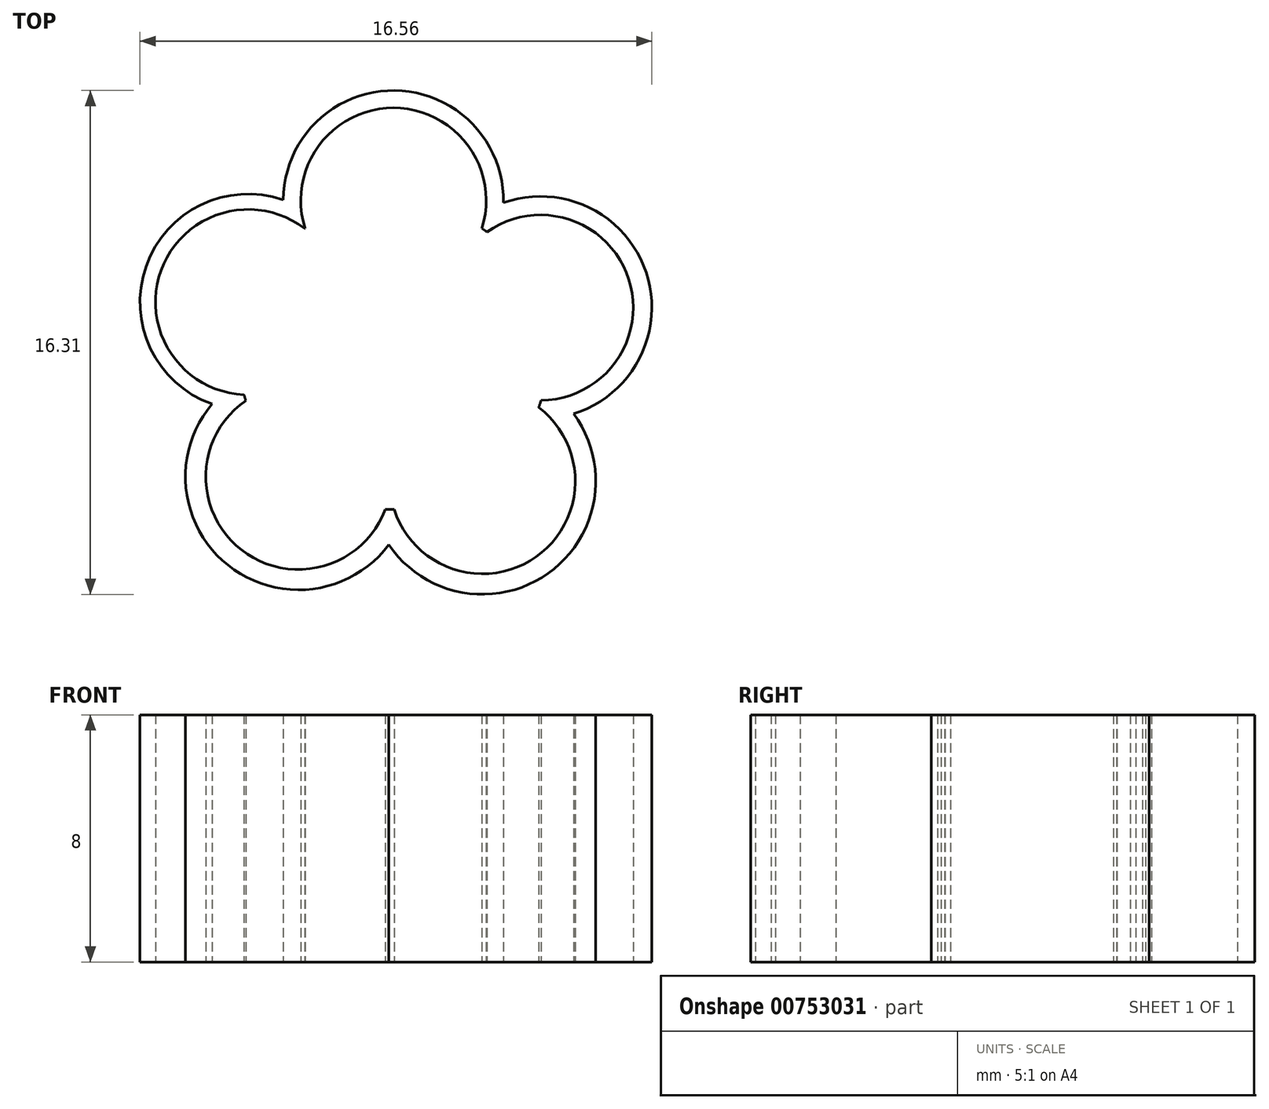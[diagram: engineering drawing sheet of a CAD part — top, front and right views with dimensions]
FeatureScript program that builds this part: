
annotation { "Feature Type Name" : "Feature", "Feature Type Description" : "" }
export const myFeature = defineFeature(function(context is Context, id is Id, definition is map)
    precondition{}
    {
        {
            var Q0;
            Q0=qCreatedBy(makeId("Top.planeOp"),FACE);
            var sketch = newSketch(context, id + "F0", { "sketchPlane" : qUnion([Q0])});
            skArc(sketch, "E0", {"start": v(-4.83, -1.29) * mm, "mid": v(-4.8, -1.38) * mm, "end": v(-4.78, -1.48) * mm});
            skArc(sketch, "E1", {"start": v(-2.85, 4.08) * mm, "mid": v(-7.51, 2.75) * mm, "end": v(-4.83, -1.29) * mm});
            skArc(sketch, "E2.trimOffspring", {"start": v(-2.86, 4.1) * mm, "mid": v(-2.87, 4.1) * mm, "end": v(-2.87, 4.1) * mm});
            skArc(sketch, "E3.trimOffspring", {"start": v(2.86, 4.1) * mm, "mid": v(-0.01, 8) * mm, "end": v(-2.85, 4.08) * mm});
            skArc(sketch, "E4.trimOffspring", {"start": v(4.78, -1.47) * mm, "mid": v(7.61, 2.45) * mm, "end": v(3.02, 3.98) * mm});
            skArc(sketch, "E5.trimOffspring", {"start": v(4.7, -1.7) * mm, "mid": v(4.74, -1.58) * mm, "end": v(4.78, -1.47) * mm});
            skArc(sketch, "E6.trimOffspring", {"start": v(3.02, 3.98) * mm, "mid": v(2.94, 4.04) * mm, "end": v(2.86, 4.1) * mm});
            skArc(sketch, "E7.trimOffspring", {"start": v(0.03, -5) * mm, "mid": v(4.61, -6.54) * mm, "end": v(4.7, -1.7) * mm});
            skArc(sketch, "E8.trimOffspring", {"start": v(-0.26, -5) * mm, "mid": v(-0.12, -5) * mm, "end": v(0.03, -5) * mm});
            skArc(sketch, "E9.trimOffspring", {"start": v(-4.78, -1.48) * mm, "mid": v(-4.91, -6.31) * mm, "end": v(-0.26, -5) * mm});
            skArc(sketch, "E10", {"start": v(-5.87, -1.59) * mm, "mid": v(-5.35, -6.8) * mm, "end": v(-0.15, -6.14) * mm});
            skArc(sketch, "E11.trimOffspring", {"start": v(-3.56, 5.02) * mm, "mid": v(-8, 2.86) * mm, "end": v(-5.87, -1.59) * mm});
            skArc(sketch, "E12.trimOffspring", {"start": v(3.56, 4.93) * mm, "mid": v(0.05, 8.56) * mm, "end": v(-3.56, 5.02) * mm});
            skArc(sketch, "E13.trimOffspring", {"start": v(5.83, -1.9) * mm, "mid": v(8.18, 2.67) * mm, "end": v(3.56, 4.93) * mm});
            skArc(sketch, "E14.trimOffspring", {"start": v(-0.15, -6.14) * mm, "mid": v(5, -7.07) * mm, "end": v(5.83, -1.9) * mm});
            skSolve(sketch);
        }
        {
            var Q0;
            {var subQ1=sQuery(id+"F0.wireOp",EDGE,"E0");Q0=makeQuery(id+"F0.imprint","IMPRINT",FACE,{"disambiguationData":[TD([[makeQuery(id+"F0.imprint","IMPRINT",EDGE,{"derivedFrom":subQ1}),-1.0]])]});}
            extrude(context, id + "F1", {"entities" : qUnion([Q0]), "depth" : 8 * mm, "offsetDistance" : 25 * mm});
        }
    });
